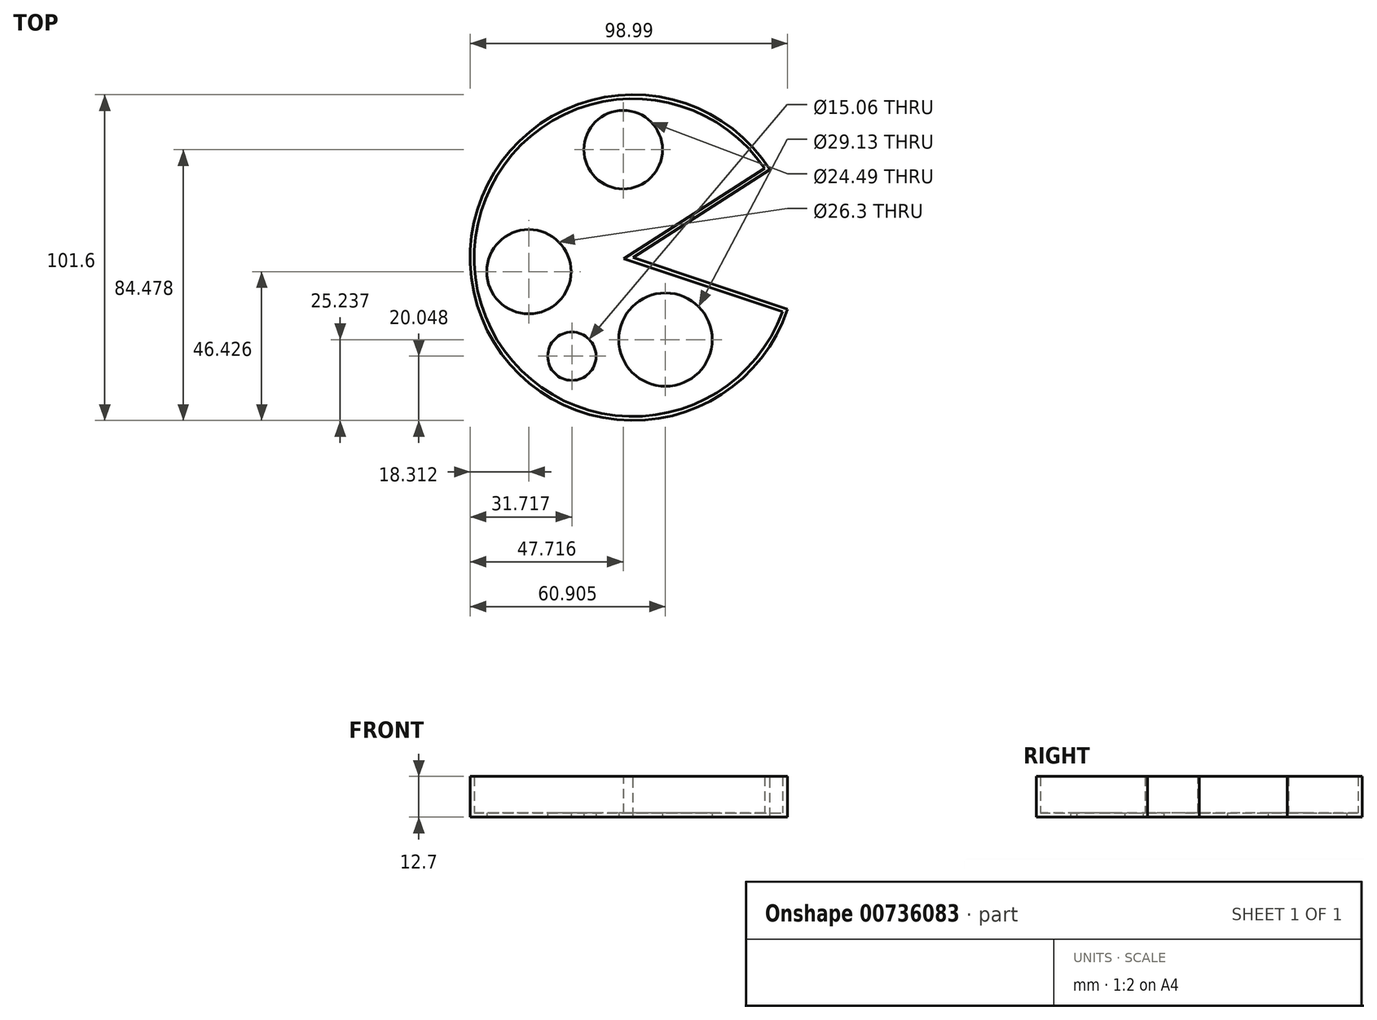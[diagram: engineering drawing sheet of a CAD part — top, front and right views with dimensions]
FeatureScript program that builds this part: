
annotation { "Feature Type Name" : "Feature", "Feature Type Description" : "" }
export const myFeature = defineFeature(function(context is Context, id is Id, definition is map)
    precondition{}
    {
        {
            var Q0;
            Q0=qCreatedBy(makeId("Top.planeOp"),FACE);
            var sketch = newSketch(context, id + "F0", { "sketchPlane" : qUnion([Q0])});
            skCircle(sketch, "E0", {"center": v(0, 0) * mm, "radius": 50.8 * mm});
            skSolve(sketch);
        }
        {
            var Q0;
            Q0=makeQuery(id+"F0.imprint","IMPRINT",FACE,{"disambiguationData":[TD([[makeQuery(id+"F0.imprint","IMPRINT",EDGE,{"derivedFrom":sQuery(id+"F0.wireOp",EDGE,"E0")}),1.0]])]});
            extrude(context, id + "F1", {"entities" : qUnion([Q0]), "depth" : 12.7 * mm, "offsetDistance" : 25.4 * mm});
        }
        {
            var Q0;
            Q0=makeQuery(id+"F1.opExtrude","CAP_FACE",FACE,{"disambiguationData":[OSD([sQuery(id+"F0.wireOp",EDGE,"E0")])],"isStart":false});
            var sketch = newSketch(context, id + "F2", { "sketchPlane" : qUnion([Q0])});
            skLineSegment(sketch, "E1", {"start": v(0, 0) * mm, "end": v(42.74, 27.46) * mm});
            skLineSegment(sketch, "E2", {"start": v(0, 0) * mm, "end": v(48.19, -16.09) * mm});
            skSolve(sketch);
        }
        {
            var Q0;
            {var subQ0=sQuery(id+"F2.wireOp",EDGE,"E1");Q0=makeQuery(id+"F2.imprint","IMPRINT",FACE,{"disambiguationData":[TD([[makeQuery(id+"F2.imprint","IMPRINT",EDGE,{"derivedFrom":subQ0}),-1.0]])]});}
            extrude(context, id + "F3", {"entities" : qUnion([Q0]), "operationType" : NewBodyOperationType.REMOVE, "oppositeDirection" : true, "depth" : 25.4 * mm, "offsetDistance" : 25.4 * mm});
        }
        {
            var Q0;
            Q0=makeQuery(id+"F1.opExtrude","CAP_FACE",FACE,{"disambiguationData":[OSD([sQuery(id+"F0.wireOp",EDGE,"E0")])],"isStart":false});
            shell(context, id + "F4", {"entities" : qUnion([Q0]), "thickness" : 1.27 * mm});
        }
        {
            var Q0;
            Q0=makeQuery(id+"F1.opExtrude","CAP_FACE",FACE,{"disambiguationData":[OSD([sQuery(id+"F0.wireOp",EDGE,"E0")])],"isStart":true});
            var sketch = newSketch(context, id + "F5", { "sketchPlane" : qUnion([Q0])});
            skCircle(sketch, "E3", {"center": v(-19.08, 30.75) * mm, "radius": 7.53 * mm});
            skCircle(sketch, "E4", {"center": v(10.1, 25.56) * mm, "radius": 14.56 * mm});
            skCircle(sketch, "E5", {"center": v(-3.08, -33.68) * mm, "radius": 12.25 * mm});
            skCircle(sketch, "E6", {"center": v(-32.49, 4.37) * mm, "radius": 13.15 * mm});
            skSolve(sketch);
        }
        {
            var Q0;
            Q0 = qSketchRegion(id + "F5", true);
            extrude(context, id + "F6", {"entities" : qUnion([Q0]), "operationType" : NewBodyOperationType.REMOVE, "oppositeDirection" : true, "depth" : 25.4 * mm, "offsetDistance" : 25.4 * mm});
        }
    });
